# Revit family: 93010.02_ms
name_source: partatom
category: Generic Models
units: mm (PartAtom-declared; Revit-internal decimal feet)

## family parameters
Always vertical = Yes
Can host rebar = No
Cut with Voids When Loaded = No
Part Type = Normal
Room Calculation Point = No
Round Connector Dimension = Use Diameter
Shared = Yes
Work Plane-Based = No

## types (1)
- 93010.02_MS
    ARTICLENO = NB
    BOMINFO = LINA
    CATALOG = KESSEL
    Default Elevation = 0 mm  [stored 0 ft]
    LINA = 93010.02/MS
    LINK = http://www.kessel.de
    Manufacturer = KESSEL
    Model = 93010.02/MS
    NB = 93010.02/MS
    NBSYN = $SA810ID03.
    NN = EasyClean free Mix & Pump grease separator
    PRC_SPECIFICATIONLINK = https://ausschreiben.de
    PROCUREDATALASTUPDATE = 2024-05-22T12:18:15.742569325+01:00
    PROCURELINK = p.caden.as/kessel/93010.02%2FMS
    PROCUREWEBLINK = https://p.caden.as
    SA100ID04 = Abscheideranlage für Fette (Schlammfang und Fettabscheider)
    SA200ID03 = free-standing set-up
    SA250ID03 = temperierte Umhausung
    SA400ID03 = PE (Polyethylen)
    SA500ID03 = Sludge trap, integrated
    SA700ID04 = Grease separator EasyClean free NS 10, Mix & Pump, SonicControl
    SA700ID05 = 10
    SA700ID06 = 1000
    SA700ID07 = 2590 mm
    SA700ID08 = 940 mm  [stored 3.08399 ft]
    SA700ID09 = 1678 mm  [stored 5.50525 ft]
    SA700ID13 = 70 mm  [stored 0.229659 ft]
    SA700ID14 = ohne Angabe
    SA700ID17 = 1255 mm  [stored 4.11745 ft]
    SA71009ID04 = 1
    SA71009ID05 = 3600 W
    SA71009ID06 = 3000 W
    SA810ID03 = 93010.02/MS
    SA810ID06 = 4026092065051
    SUPPLIER = KESSEL

note: [stored X ft] marks values corroborated as IEEE doubles in the binary element streams (Revit-internal decimal feet)

## geometry (parser evidence)
native form markers: Sweep x19
no freeform markers — native parametric forms only
